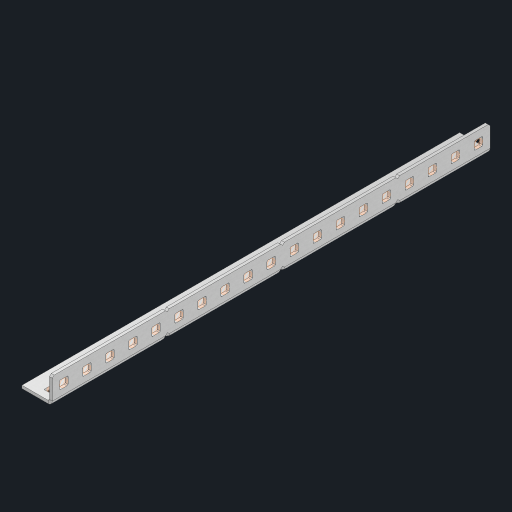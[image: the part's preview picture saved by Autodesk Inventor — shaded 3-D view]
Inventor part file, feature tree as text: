
AUTODESK INVENTOR PART (.ipt)
format: ipt  version: 2023 (Build 270158000, 158)  size: 747,520 bytes
history: native  units: in
note: dims shown in document units (in); Inventor stores cm internally (conversion verified against a paired STEP export)
features: other x43, extrude x37, sheet_metal_op x10, sketch x8, mirror x1, pattern_linear x1, chamfer x1
ambient origin geometry x8: Origin, YZ Plane, XZ Plane, XY Plane, X Axis, Y Axis, Z Axis, Center Point
bodies: Solid1 (feature_tree), Body (feature_tree)
feature tree (101):
  other  "Flange Pattern Plane"
  sheet_metal_op  "Flange Pattern"
  sheet_metal_op  "Body Pattern"
  other  "Arc Length"
  mirror  "Notch Mirror"
  pattern_linear  "Notch Pattern"  Spacing1=0.25in  [1 undecoded]
  chamfer  "End Chamfer"
  extrude  "Half Cut"  Depth=0.0625in
  sketch  "Sketch1"  dims[d0=1.5in]
  other  "Plate1"
  sketch  "Sketch2"  dims[d1=9.5in]
  other  "Plate2"
  sheet_metal_op  "Bend1"
  sheet_metal_op  "Corner1"
  sketch  "Sketch3"  dims[d2=0.0625in]
  other  "Flange Pattern Sketch"
  sketch  "Sketch7"  dims[d3=0.0625in]
  other  "Srf1"
  other  "Srf2"
  sketch  "Sketch8"  dims[d4=0.0312in]
  sketch  "Sketch9"  dims[d5=0.125in]
  other  "Srf91"
  sheet_metal_op  "Body Pattern Sketch"
  other  "Srf92"
  sketch  "Sketch13"  dims[d6=0.0625in]
  sketch  "Sketch14"  dims[d7=0.5in d8=90.0deg d9=0.0312in d10=0.25in d11=0.0625in d12=0.0625in d16=0.182in d17=0.02in d18=0.0625in d19=0.0in d20=0.25in d21=0.25in d46=0.172in d47=1.0in d48=0.0in d49=0.182in d50=0.02in d51=0.25in d52=0.25in d53=0.0625in d54=0.0in d55=0.172in d56=1.0in d57=0.0in d60=7.4803in d62=0.5in d63=0.3937in d65=0.5in d85=0.1473in d86=0.1782in d88=0.04in d89=0.0625in d90=0.0in d91=0.04in d92=0.0491in d95=2.5in d96=0.04in d97=0.25in d98=45.0deg d101=0.0in d102=2.497in d131=0.5in d132=7.4803in d134=0.5in d139=0.5in]
  other  "Srf856"
  other  "Srf1310"
  other  "Srf1311"
  other  "Srf1312"
  other  "Srf1376"
  other  "Srf1377"
  other  "Srf1728"
  other  "Srf1755"
  other  "Srf1878"
  other  "Srf1879"
  other  "Srf1880"
  other  "Srf1881"
  other  "Srf1882"
  other  "Srf1883"
  other  "Srf1884"
  other  "Srf1885"
  other  "Srf1886"
  other  "Srf1887"
  other  "Srf1888"
  other  "Srf1889"
  other  "Srf1890"
  other  "Srf1942"
  other  "Srf1943"
  other  "Srf1944"
  other  "Srf1945"
  other  "Srf1946"
  other  "Srf1947"
  other  "Srf1948"
  other  "Srf1949"
  other  "Srf1950"
  other  "Srf1951"
  other  "Srf1952"
  other  "Srf1953"
  other  "Srf1954"
  sheet_metal_op  "Flange Stamp"
  sheet_metal_op  "Flange Circle"
  sheet_metal_op  "Body Stamp"
  sheet_metal_op  "Body Circle"
  sheet_metal_op  "Notch"
  extrude  "ExtrusionSrf2"  Depth=0.0625in
  extrude  "ExtrusionSrf92"  Depth=0.5in
  extrude  "ExtrusionSrf856"  Depth=0.02in
  extrude  "ExtrusionSrf1310"  Depth=0.0625in
  extrude  "ExtrusionSrf1311"  TaperAngle=0.0deg  [1 undecoded]
  extrude  "ExtrusionSrf1312"  Depth=0.5in
  extrude  "ExtrusionSrf1376"  Depth=0.5in
  extrude  "ExtrusionSrf1377"  Depth=0.5in
  extrude  "ExtrusionSrf1728"  Depth=0.5in TaperAngle=0.0deg
  extrude  "ExtrusionSrf1755"  Depth=0.5in
  extrude  "ExtrusionSrf1878"  Depth=0.02in
  extrude  "ExtrusionSrf1879"  Depth=0.5in
  extrude  "ExtrusionSrf1880"  Depth=0.5in
  extrude  "ExtrusionSrf1881"  Depth=0.0625in
  extrude  "ExtrusionSrf1882"  TaperAngle=0.0deg  [1 undecoded]
  extrude  "ExtrusionSrf1883"  Depth=0.5in
  extrude  "ExtrusionSrf1884"  Depth=0.5in TaperAngle=0.0deg
  extrude  "ExtrusionSrf1885"  Depth=0.5in
  extrude  "ExtrusionSrf1886"  Depth=0.5in
  extrude  "ExtrusionSrf1887"  Depth=0.5in
  extrude  "ExtrusionSrf1888"  Depth=0.5in
  extrude  "ExtrusionSrf1889"  Depth=0.5in
  extrude  "ExtrusionSrf1890"  Depth=0.0625in
  extrude  "ExtrusionSrf1942"  TaperAngle=0.0deg  [1 undecoded]
  extrude  "ExtrusionSrf1943"  Depth=0.5in
  extrude  "ExtrusionSrf1944"  Depth=0.5in
  extrude  "ExtrusionSrf1945"  Depth=0.5in
  extrude  "ExtrusionSrf1946"  Depth=0.5in TaperAngle=45.0deg
  extrude  "ExtrusionSrf1947"  TaperAngle=0.0deg  [1 undecoded]
  extrude  "ExtrusionSrf1948"  Depth=0.5in
  extrude  "ExtrusionSrf1949"  Depth=0.5in
  extrude  "ExtrusionSrf1950"  Depth=0.5in
  extrude  "ExtrusionSrf1951"  Depth=0.5in
  extrude  "ExtrusionSrf1952"  Depth=0.5in
  extrude  "ExtrusionSrf1953"  [1 undecoded]
  extrude  "ExtrusionSrf1954"  [1 undecoded]
note: 7 required parameter values undecoded (feature->parameter linkage not recoverable at this tier; creation-order binding heuristic only, values carry confidence <= 0.55)
